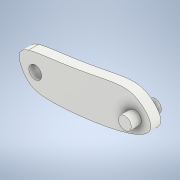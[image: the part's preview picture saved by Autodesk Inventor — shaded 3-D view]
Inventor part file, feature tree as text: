
AUTODESK INVENTOR PART (.ipt)
format: ipt  version: 2022 (Build 260153000, 153)  size: 127,488 bytes
history: native  units: in
note: dims shown in document units (in); Inventor stores cm internally (conversion verified against a paired STEP export)
features: extrude x3, sketch x2, projected_geometry x1
ambient origin geometry x8: Origin, YZ Plane, XZ Plane, XY Plane, X Axis, Y Axis, Z Axis, Center Point
bodies: Solid1 (feature_tree)
feature tree (6):
  sketch  "Sketch2"  dims[d0=0.1969in d1=0.0in d2=0.1969in d3=0.0in]
  extrude  "Extrusion1"  Depth=0.1969in TaperAngle=0.0deg
  extrude  "Extrusion2"  [1 undecoded]
  extrude  "Extrusion3"  [1 undecoded]
  sketch  "Sketch3"  dims[d4=0.1969in d5=0.0in]
  projected_geometry  "Projected Loop2"
note: 2 required parameter values undecoded (feature->parameter linkage not recoverable at this tier; creation-order binding heuristic only, values carry confidence <= 0.55)
